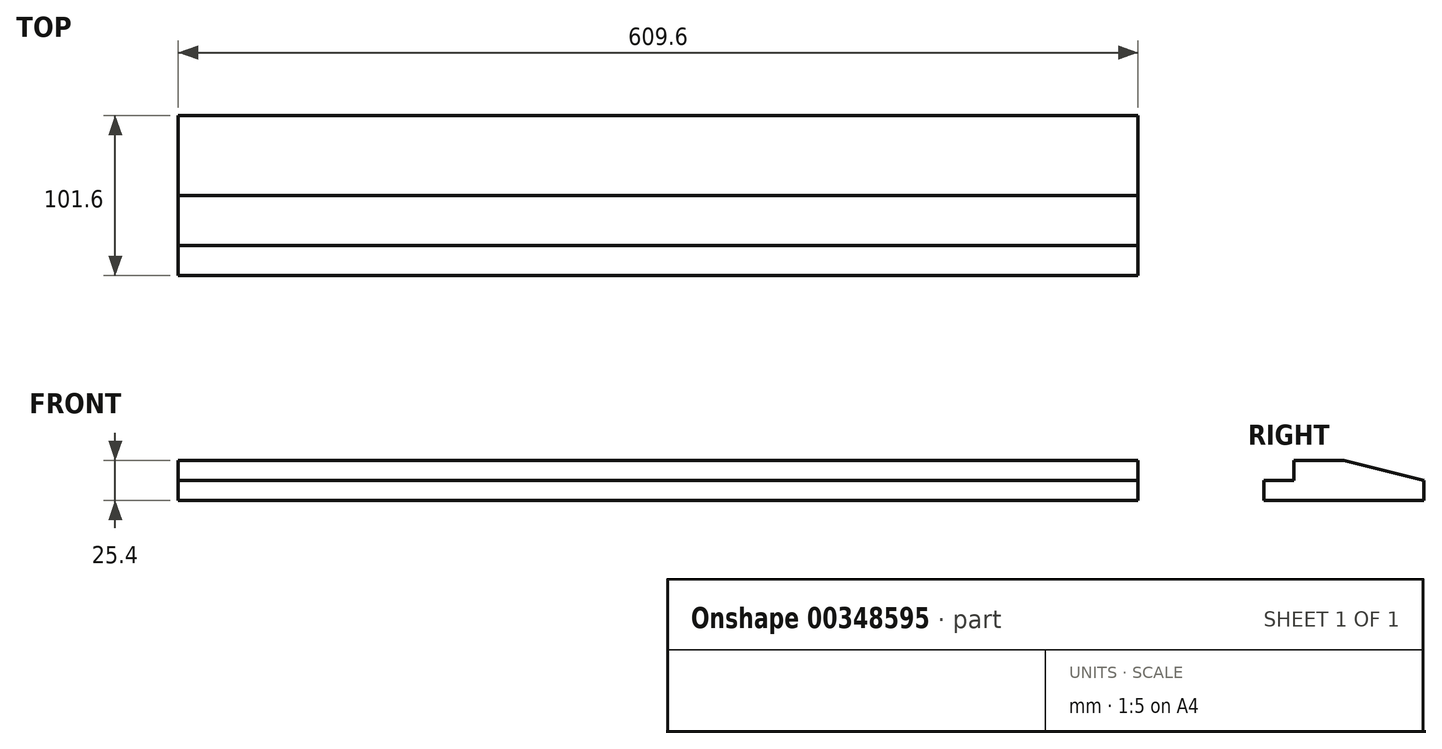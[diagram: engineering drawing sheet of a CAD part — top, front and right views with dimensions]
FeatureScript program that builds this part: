
annotation { "Feature Type Name" : "Feature", "Feature Type Description" : "" }
export const myFeature = defineFeature(function(context is Context, id is Id, definition is map)
    precondition{}
    {
        {
            var Q0;
            Q0=qCreatedBy(makeId("Top.planeOp"),FACE);
            var sketch = newSketch(context, id + "F0", { "sketchPlane" : qUnion([Q0])});
            skLineSegment(sketch, "E0.bottom", {"start": v(-308.7, 92.41) * mm, "end": v(300.9, 92.41) * mm});
            skLineSegment(sketch, "E0.top", {"start": v(-308.7, -9.19) * mm, "end": v(300.9, -9.19) * mm});
            skLineSegment(sketch, "E0.left", {"start": v(-308.7, 92.41) * mm, "end": v(-308.7, -9.19) * mm});
            skLineSegment(sketch, "E0.right", {"start": v(300.9, 92.41) * mm, "end": v(300.9, -9.19) * mm});
            skLineSegment(sketch, "E1", {"start": v(-308.7, 9.86) * mm, "end": v(300.9, 9.86) * mm});
            skSolve(sketch);
        }
        {
            var Q0;
            {var subQ0=sQuery(id+"F0.wireOp",EDGE,"E0.bottom");Q0=makeQuery(id+"F0.imprint","IMPRINT",FACE,{"disambiguationData":[TD([[makeQuery(id+"F0.imprint","IMPRINT",EDGE,{"derivedFrom":subQ0}),-1.0]])]});}
            extrude(context, id + "F1", {"entities" : qUnion([Q0]), "depth" : 12.7 * mm});
        }
        {
            var Q0;
            Q0=qSketchRegion(id+"F0",true);
            var Q1;
            Q1=makeQuery(id+"F1.opExtrude","CAP_FACE",FACE,{"disambiguationData":[OSD([sQuery(id+"F0.wireOp",EDGE,"E0.bottom"),sQuery(id+"F0.wireOp",EDGE,"E0.left"),sQuery(id+"F0.wireOp",EDGE,"E0.right"),sQuery(id+"F0.wireOp",EDGE,"E1")])],"isStart":false});
            extrude(context, id + "F2", {"entities" : qUnion([Q0, Q1]), "operationType" : NewBodyOperationType.ADD, "depth" : 12.7 * mm});
        }
        {
            var Q0;
            {var subQ0=sQuery(id+"F0.wireOp",EDGE,"E0.bottom");Q0=makeQuery(id+"F2.opExtrude","CAP_EDGE",EDGE,{"disambiguationData":[OSD([subQ0]),TDD([makeQuery(id+"F1.opExtrude","CAP_EDGE",EDGE,{"disambiguationData":[OSD([subQ0])],"isStart":false})])],"isStart":false});}
            chamfer(context, id + "F3", {"entities" : qUnion([Q0]), "chamferType" : ChamferType.TWO_OFFSETS, "width1" : 12.7 * mm, "oppositeDirection" : false, "width2" : 50.8 * mm, "tangentPropagation" : true});
        }
    });
